# Revit family: Maxlogic Оповещатель звуковой, светозвуковой адресный для совмещенного монтажа с автоматическим пожарным извещателем
name_source: partatom
category: Fire Alarm Devices
units: mm (PartAtom-declared; Revit-internal decimal feet)

## family parameters
Cut with Voids When Loaded = No
Host = Face
Maintain Annotation Orientation = Yes
OmniClass Number = 23.85.30.21
OmniClass Title = Environmental Detection/Registration
Part Type = Normal
Room Calculation Point = No
Round Connector Dimension = Use Diameter
Shared = No

## types (2) — shared parameters
Manufacturer = Mavili Elektronik Ticaret A.Ş.
Model = Maxlogic
URL = https://www.mavili.com.tr
Адрес №1 = Şerifali Mahallesi Kutup Sokak No:27/1-2-4 Ümraniye TR-34775 İSTANBUL
Вторичный материал = Пластмассовый
Гарантийный срок = Года
Гарантийный срок запчастей = 2
Гарантия срока службы = 2
Главный Материал = Белый пластмассовый ABS
Инструкция по установке = https://mavilielektronik.com
Класс защиты = IP 21C
Монтажная поверхность = Потолочная
Настройка адреса устройства = Модульная адресация
Номер телефона = (+)90 216 466 45 05
Номер факса = (+)90 216 466 45 10
Номинальная высота = 114 мм
Номинальная глубина = 32 мм
Номинальная ширина = 114 мм
Рабочая Температура = (-10°C) - (+55°C)
Рабочее напряжение (по умолчанию) = 24 В Пост. ток
Цвет = Белый
zero-valued in all types: Cost, Default Elevation

## per-type parameters (varying)
| type | Description | Вес | Диапазон рабочего напряжения | Код продукта | Производительность кода |
| Maxlogic Оповещатель звуковой адресный для совмещенного монтажа с автоматическим пожарным извещателем | Оповещатель звуковой адресный для совмещенного монтажа с автоматическим пожарным извещателем | 120 гр | 18-33 В Пост. ток | ML-1101 | EN 54-3 |
| Maxlogic Оповещатель светозвуковой адресный для совмещенного монтажа с автоматическим пожарным извещателем | Оповещатель светозвуковой адресный для совмещенного монтажа с автоматическим пожарным извещателем | 140 гр | 18-33В Пост. ток | ML-1102 | EN 54-3 / EN 54-23 |

## geometry (parser evidence)
native form markers: Sweep x2
no freeform markers — native parametric forms only
